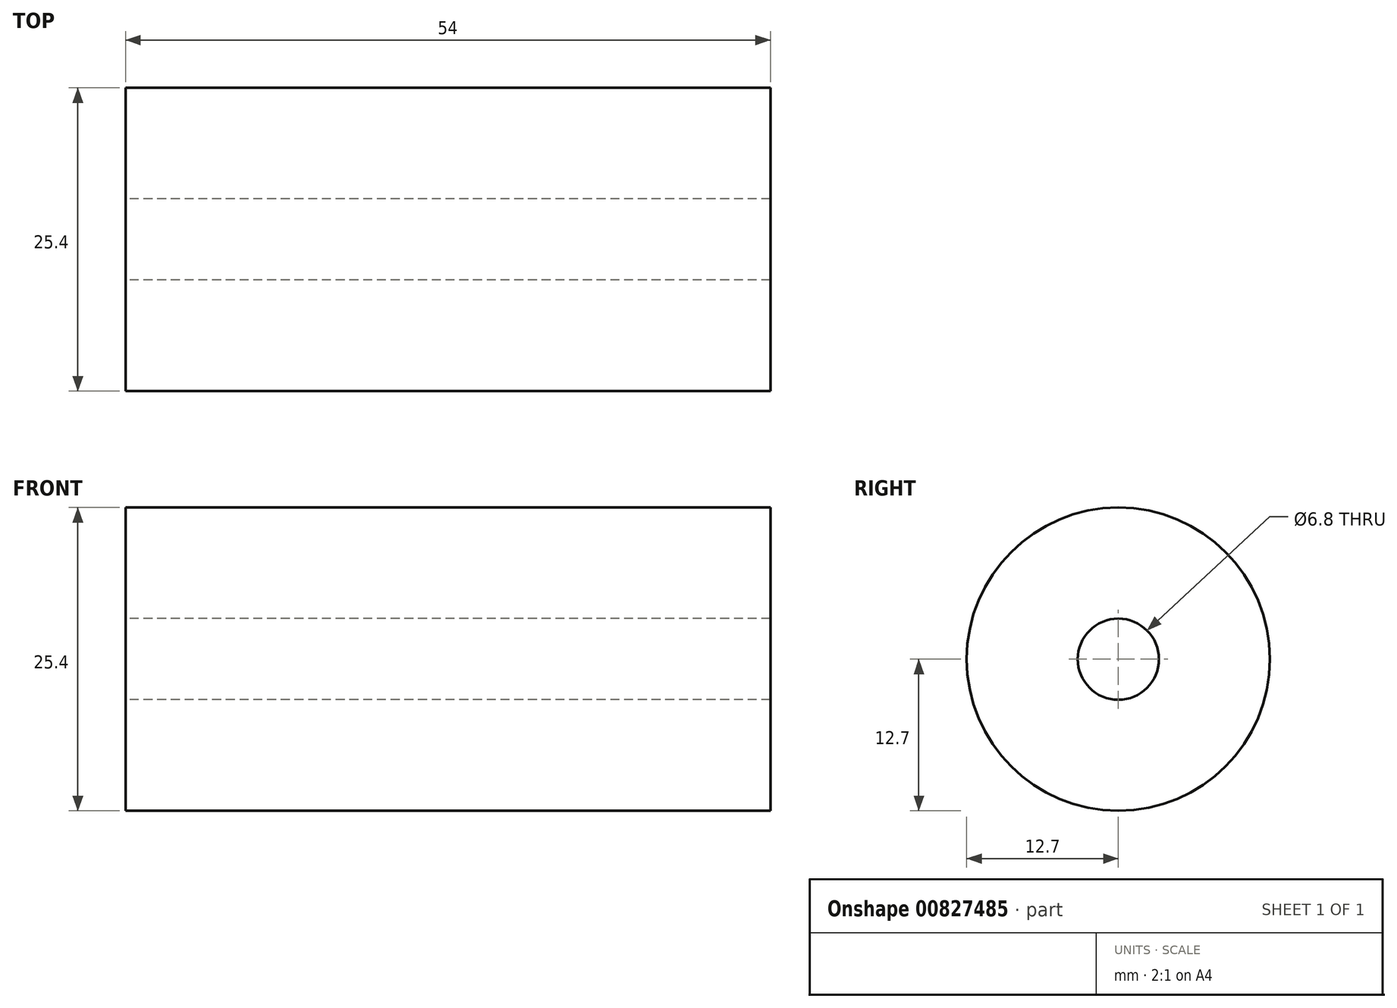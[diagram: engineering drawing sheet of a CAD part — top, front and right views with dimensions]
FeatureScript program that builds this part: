
annotation { "Feature Type Name" : "Feature", "Feature Type Description" : "" }
export const myFeature = defineFeature(function(context is Context, id is Id, definition is map)
    precondition{}
    {
        {
            var Q0;
            Q0=qCreatedBy(makeId("Right.planeOp"),FACE);
            var sketch = newSketch(context, id + "F0", { "sketchPlane" : qUnion([Q0])});
            skCircle(sketch, "E0", {"center": v(0, 0) * mm, "radius": 12.7 * mm});
            skSolve(sketch);
        }
        {
            var Q0;
            Q0 = qSketchRegion(id + "F0", true);
            extrude(context, id + "F1", {"entities" : qUnion([Q0]), "depth" : 54 * mm, "offsetDistance" : 25 * mm});
        }
        {
            var Q0;
            Q0=qCreatedBy(makeId("Right.planeOp"),FACE);
            var sketch = newSketch(context, id + "F2", { "sketchPlane" : qUnion([Q0])});
            skPoint(sketch, "E1", {"position": v(0, 0) * mm});
            skSolve(sketch);
        }
        {
            var Q0;
            Q0=sQuery(id+"F2.wireOp",VERTEX,"E1");
            var Q1;
            Q1=makeQuery(id+"F1.opExtrude","SWEPT_BODY",BODY,{"disambiguationData":[OSD([sQuery(id+"F0.wireOp",EDGE,"E0")])]});
            hole(context, id + "F3", {"style" : HoleStyle.SIMPLE, "endStyle" : HoleEndStyle.THROUGH, "oppositeDirection" : true, "standardTappedOrClearance" : lookupTablePath({ "standard" : "ISO", "engagement" : "75%", "pitch" : "1.25 mm", "size" : "M8", "type" : "Tapped" }), "standardBlindInLast" : lookupTablePath({ "standard" : "ISO", "engagement" : "75%", "pitch" : "1.25 mm", "size" : "M8", "type" : "Tapped" }), "holeDiameter" : 6.8 * mm, "majorDiameter" : 8 * mm, "showTappedDepth" : true, "isTappedThrough" : true, "tappedDepth" : 12 * mm, "tapClearance" : 3, "locations" : qUnion([Q0]), "scope" : qUnion([Q1])});
        }
    });
